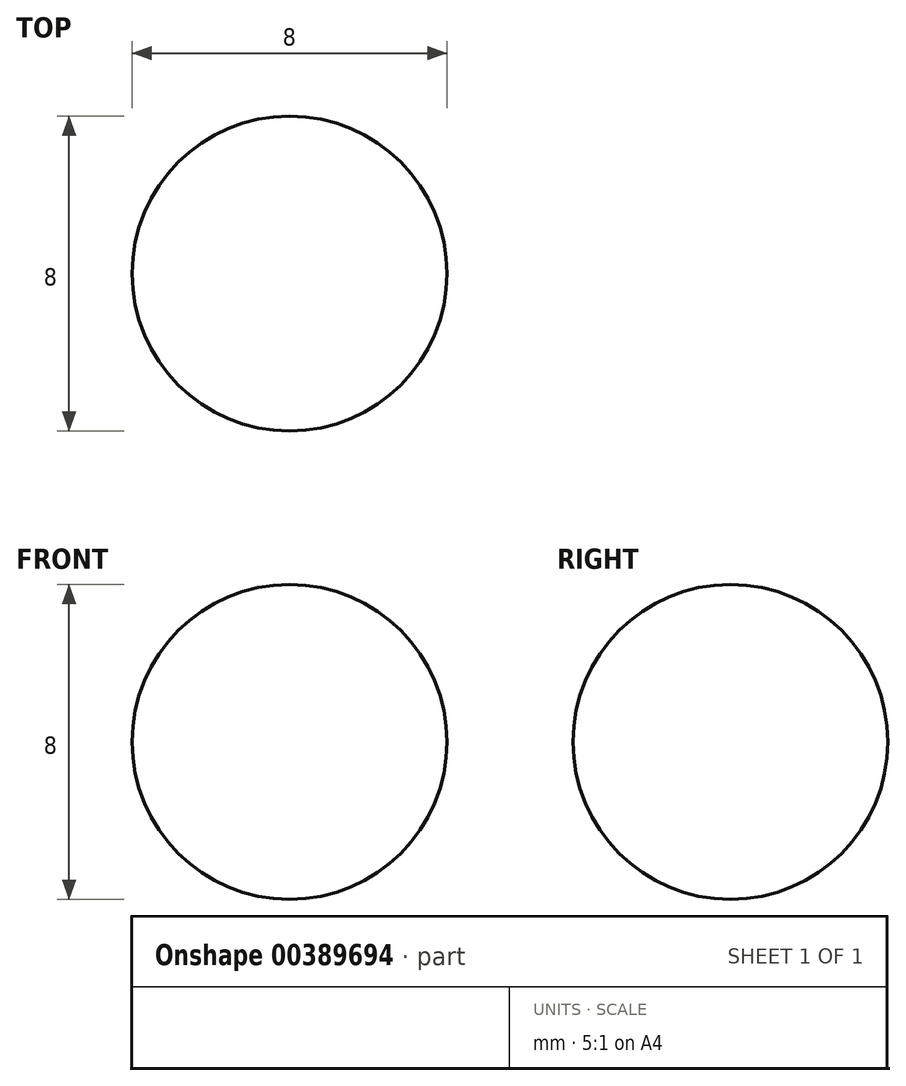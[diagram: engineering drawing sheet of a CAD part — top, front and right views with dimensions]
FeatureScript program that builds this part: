
annotation { "Feature Type Name" : "Feature", "Feature Type Description" : "" }
export const myFeature = defineFeature(function(context is Context, id is Id, definition is map)
    precondition{}
    {
        {
            var Q0;
            Q0=qCreatedBy(makeId("Front.planeOp"),FACE);
            var sketch = newSketch(context, id + "F0", { "sketchPlane" : qUnion([Q0])});
            skCircle(sketch, "E0", {"center": v(0, 0) * mm, "radius": 4 * mm});
            skLineSegment(sketch, "E1", {"start": v(0, 0) * mm, "end": v(0, 5.9) * mm});
            skLineSegment(sketch, "E2", {"start": v(0, 0) * mm, "end": v(0, -5.7) * mm});
            skSolve(sketch);
        }
        {
            var Q0;
            {var subQ0=sQuery(id+"F0.wireOp",EDGE,"E1");var subQ1=sQuery(id+"F0.wireOp",EDGE,"E0");var subQ2=makeQuery(id+"F0.imprint","INTERSECT",VERTEX,{"derivedFrom":[subQ1,subQ0]});Q0=makeQuery(id+"F0.imprint","IMPRINT",FACE,{"disambiguationData":[TD([[makeQuery(id+"F0.imprint","IMPRINT",EDGE,{"disambiguationData":[TD([[subQ2,-1.0]])],"derivedFrom":subQ1}),1.0]])]});}
            var Q1;
            Q1=sQuery(id+"F0.wireOp",EDGE,"E1");
            revolve(context, id + "F1", {"entities" : qUnion([Q0]), "axis" : qUnion([Q1]), "revolveType" : RevolveType.FULL});
        }
    });
